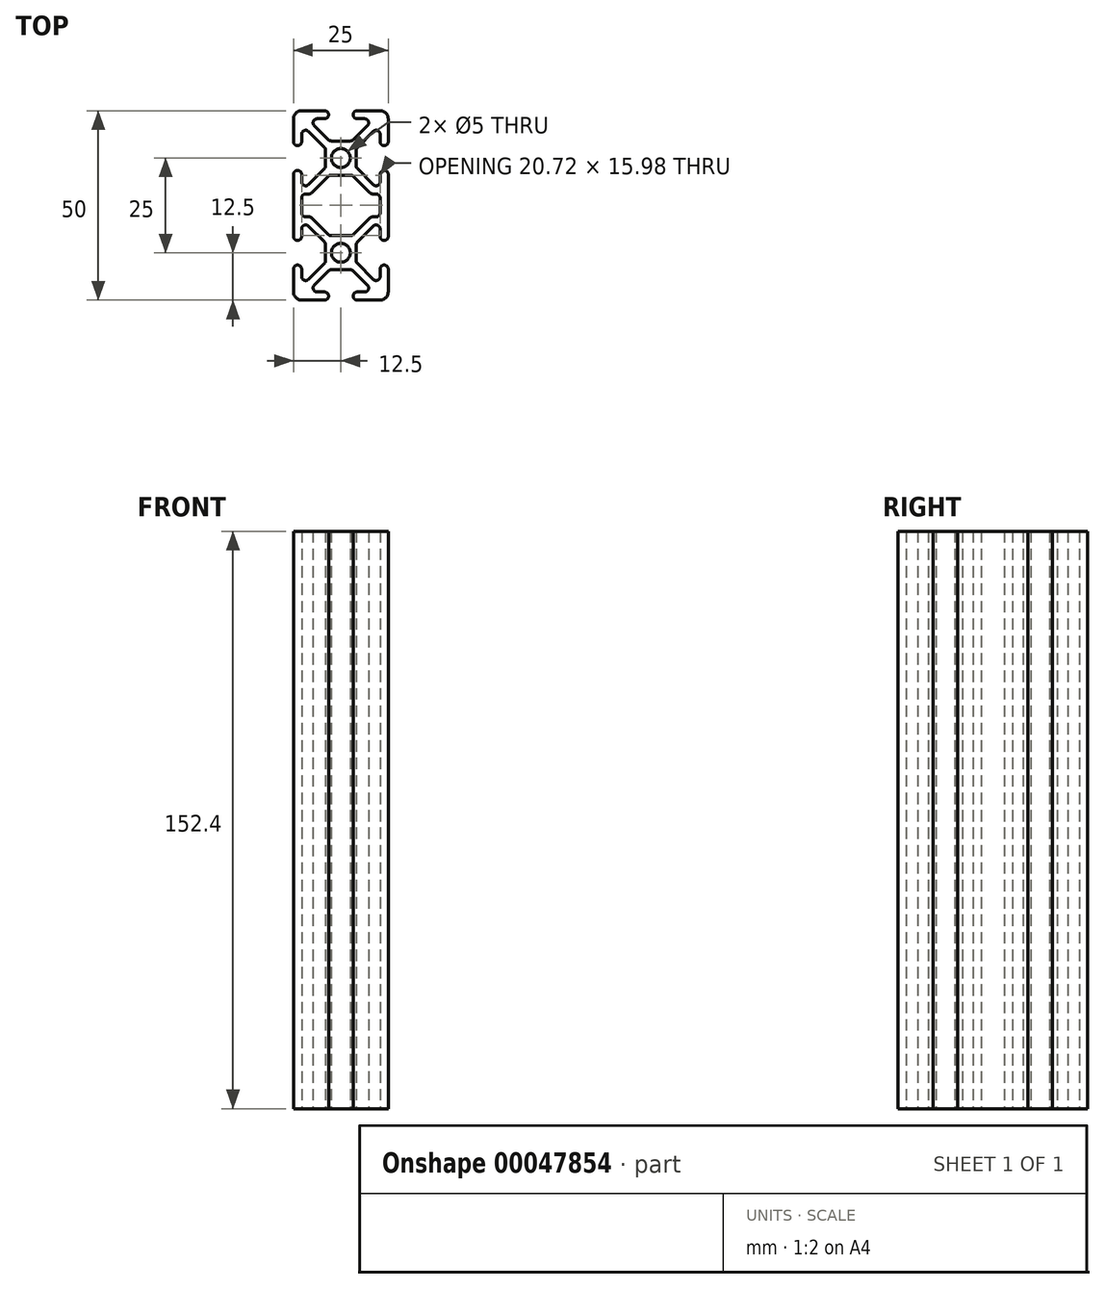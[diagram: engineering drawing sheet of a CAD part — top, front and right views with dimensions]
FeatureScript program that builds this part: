
annotation { "Feature Type Name" : "Feature", "Feature Type Description" : "" }
export const myFeature = defineFeature(function(context is Context, id is Id, definition is map)
    precondition{}
    {
        {
            var Q0;
            Q0=qCreatedBy(makeId("Top.planeOp"),FACE);
            var sketch = newSketch(context, id + "F0", { "sketchPlane" : qUnion([Q0])});
            skCircle(sketch, "E0", {"center": v(0, 0) * mm, "radius": 2.5 * mm});
            skLineSegment(sketch, "E1", {"start": v(0, 0) * mm, "end": v(0, 4.5) * mm, "construction": true});
            skLineSegment(sketch, "E2", {"start": v(0, 0) * mm, "end": v(-4.05, 0) * mm, "construction": true});
            skLineSegment(sketch, "E3", {"start": v(0, 0) * mm, "end": v(-12.5, 12.5) * mm, "construction": true});
            skLineSegment(sketch, "E4", {"start": v(-12.5, 10.36) * mm, "end": v(-12.5, 4.32) * mm});
            skLineSegment(sketch, "E5", {"start": v(-10.36, 12.5) * mm, "end": v(-4.32, 12.5) * mm});
            skLineSegment(sketch, "E6", {"start": v(-4.32, 10.36) * mm, "end": v(-6.26, 10.36) * mm});
            skLineSegment(sketch, "E7", {"start": v(-10.36, 6.26) * mm, "end": v(-10.36, 4.32) * mm});
            skArc(sketch, "E8", {"start": v(-4.32, 12.5) * mm, "mid": v(-3.25, 11.43) * mm, "end": v(-4.32, 10.36) * mm});
            skArc(sketch, "E9", {"start": v(-10.36, 4.32) * mm, "mid": v(-11.43, 3.25) * mm, "end": v(-12.5, 4.32) * mm});
            skLineSegment(sketch, "E10", {"start": v(0, 4.5) * mm, "end": v(-2.55, 4.5) * mm});
            skLineSegment(sketch, "E11", {"start": v(-4.05, 2.1) * mm, "end": v(-4.05, 0) * mm});
            skLineSegment(sketch, "E12", {"start": v(-8.53, 7.02) * mm, "end": v(-4.36, 2.85) * mm});
            skLineSegment(sketch, "E13", {"start": v(-7.02, 8.53) * mm, "end": v(-3.31, 4.82) * mm});
            skLineSegment(sketch, "E14.0.MirrorCS", {"start": v(10.36, 6.26) * mm, "end": v(10.36, 4.32) * mm});
            skLineSegment(sketch, "E14.1.MirrorCS", {"start": v(7.02, 8.53) * mm, "end": v(3.31, 4.82) * mm});
            skArc(sketch, "E14.2.MirrorCS", {"start": v(4.32, 12.5) * mm, "mid": v(3.25, 11.43) * mm, "end": v(4.32, 10.36) * mm});
            skArc(sketch, "E14.3.MirrorCS", {"start": v(10.36, 4.32) * mm, "mid": v(11.43, 3.25) * mm, "end": v(12.5, 4.32) * mm});
            skLineSegment(sketch, "E14.4.MirrorCS", {"start": v(10.36, 12.5) * mm, "end": v(4.32, 12.5) * mm});
            skLineSegment(sketch, "E14.5.MirrorCS", {"start": v(4.32, 10.36) * mm, "end": v(6.26, 10.36) * mm});
            skLineSegment(sketch, "E14.6.MirrorCS", {"start": v(12.5, 10.36) * mm, "end": v(12.5, 4.32) * mm});
            skLineSegment(sketch, "E14.7.MirrorCS", {"start": v(8.53, 7.02) * mm, "end": v(4.36, 2.85) * mm});
            skLineSegment(sketch, "E15.0.MirrorCS", {"start": v(0, 4.5) * mm, "end": v(2.55, 4.5) * mm});
            skLineSegment(sketch, "E16.0.MirrorCS", {"start": v(4.05, 2.1) * mm, "end": v(4.05, 0) * mm});
            skLineSegment(sketch, "E17.1.MirrorCS", {"start": v(12.5, -12.5) * mm, "end": v(12.5, -4.32) * mm});
            skLineSegment(sketch, "E17.5.MirrorCS", {"start": v(10.36, -6.26) * mm, "end": v(10.36, -4.32) * mm});
            skLineSegment(sketch, "E17.6.MirrorCS", {"start": v(8.53, -7.02) * mm, "end": v(4.36, -2.85) * mm});
            skArc(sketch, "E17.10.MirrorCS", {"start": v(10.36, -4.32) * mm, "mid": v(11.43, -3.25) * mm, "end": v(12.5, -4.32) * mm});
            skLineSegment(sketch, "E17.11.MirrorCS", {"start": v(-12.5, -12.5) * mm, "end": v(-12.5, -4.32) * mm});
            skLineSegment(sketch, "E17.14.MirrorCS", {"start": v(-8.53, -7.02) * mm, "end": v(-4.36, -2.85) * mm});
            skArc(sketch, "E17.15.MirrorCS", {"start": v(-10.36, -4.32) * mm, "mid": v(-11.43, -3.25) * mm, "end": v(-12.5, -4.32) * mm});
            skLineSegment(sketch, "E17.16.MirrorCS", {"start": v(-10.36, -6.26) * mm, "end": v(-10.36, -4.32) * mm});
            skLineSegment(sketch, "E18.0.MirrorCS", {"start": v(4.05, -2.1) * mm, "end": v(4.05, 0) * mm});
            skLineSegment(sketch, "E19.0.MirrorCS", {"start": v(-4.05, -2.1) * mm, "end": v(-4.05, 0) * mm});
            skPoint(sketch, "E20.visualSharp", {"position": v(-12.5, 12.5) * mm});
            skArc(sketch, "E20.filletArc", {"start": v(-10.36, 12.5) * mm, "mid": v(-11.87, 11.87) * mm, "end": v(-12.5, 10.36) * mm});
            skPoint(sketch, "E21.visualSharp", {"position": v(12.5, 12.5) * mm});
            skArc(sketch, "E21.filletArc", {"start": v(12.5, 10.36) * mm, "mid": v(11.87, 11.87) * mm, "end": v(10.36, 12.5) * mm});
            skPoint(sketch, "E22.visualSharp", {"position": v(-12.5, -12.5) * mm});
            skPoint(sketch, "E23.visualSharp", {"position": v(4.05, 4.5) * mm});
            skPoint(sketch, "E24.visualSharp", {"position": v(-10.36, 8.85) * mm});
            skArc(sketch, "E24.filletArc", {"start": v(-8.53, 7.02) * mm, "mid": v(-9.7, 7.25) * mm, "end": v(-10.36, 6.26) * mm});
            skPoint(sketch, "E25.visualSharp", {"position": v(-8.85, 10.36) * mm});
            skArc(sketch, "E25.filletArc", {"start": v(-6.26, 10.36) * mm, "mid": v(-7.25, 9.7) * mm, "end": v(-7.02, 8.53) * mm});
            skPoint(sketch, "E26.visualSharp", {"position": v(8.85, 10.36) * mm});
            skArc(sketch, "E26.filletArc", {"start": v(7.02, 8.53) * mm, "mid": v(7.25, 9.7) * mm, "end": v(6.26, 10.36) * mm});
            skArc(sketch, "E27.filletArc", {"start": v(10.36, 6.26) * mm, "mid": v(9.7, 7.25) * mm, "end": v(8.53, 7.02) * mm});
            skArc(sketch, "E28.filletArc", {"start": v(8.53, -7.02) * mm, "mid": v(9.7, -7.25) * mm, "end": v(10.36, -6.26) * mm});
            skArc(sketch, "E29.filletArc", {"start": v(-10.36, -6.26) * mm, "mid": v(-9.7, -7.25) * mm, "end": v(-8.53, -7.02) * mm});
            skPoint(sketch, "E30.orphan", {"position": v(-4.05, 4.5) * mm});
            skPoint(sketch, "E31.visualSharp", {"position": v(-3, 4.5) * mm});
            skArc(sketch, "E31.filletArc", {"start": v(-3.31, 4.82) * mm, "mid": v(-2.96, 4.6) * mm, "end": v(-2.55, 4.5) * mm});
            skPoint(sketch, "E32.visualSharp", {"position": v(3, 4.5) * mm});
            skArc(sketch, "E32.filletArc", {"start": v(2.55, 4.5) * mm, "mid": v(2.96, 4.6) * mm, "end": v(3.31, 4.82) * mm});
            skPoint(sketch, "E33.visualSharp", {"position": v(-4.05, 2.54) * mm});
            skArc(sketch, "E33.filletArc", {"start": v(-4.05, 2.1) * mm, "mid": v(-4.13, 2.5) * mm, "end": v(-4.36, 2.85) * mm});
            skPoint(sketch, "E34.visualSharp", {"position": v(-4.05, -2.54) * mm});
            skArc(sketch, "E34.filletArc", {"start": v(-4.36, -2.85) * mm, "mid": v(-4.13, -2.5) * mm, "end": v(-4.05, -2.1) * mm});
            skPoint(sketch, "E35.visualSharp", {"position": v(4.05, -2.54) * mm});
            skArc(sketch, "E35.filletArc", {"start": v(4.05, -2.1) * mm, "mid": v(4.13, -2.5) * mm, "end": v(4.36, -2.85) * mm});
            skPoint(sketch, "E36.visualSharp", {"position": v(4.05, 2.54) * mm});
            skArc(sketch, "E36.filletArc", {"start": v(4.36, 2.85) * mm, "mid": v(4.13, 2.5) * mm, "end": v(4.05, 2.1) * mm});
            skCircle(sketch, "E37", {"center": v(0, -25) * mm, "radius": 2.5 * mm});
            skLineSegment(sketch, "E38", {"start": v(0, 0) * mm, "end": v(0, -25) * mm, "construction": true});
            skLineSegment(sketch, "E39", {"start": v(0, -12.5) * mm, "end": v(3.65, -12.5) * mm, "construction": true});
            skArc(sketch, "E40.0.MirrorCS", {"start": v(2.55, -29.51) * mm, "mid": v(2.96, -29.6) * mm, "end": v(3.31, -29.82) * mm});
            skArc(sketch, "E40.1.MirrorCS", {"start": v(4.36, -27.85) * mm, "mid": v(4.13, -27.5) * mm, "end": v(4.05, -27.1) * mm});
            skArc(sketch, "E40.2.MirrorCS", {"start": v(-4.05, -27.1) * mm, "mid": v(-4.13, -27.5) * mm, "end": v(-4.36, -27.85) * mm});
            skArc(sketch, "E40.3.MirrorCS", {"start": v(-4.36, -22.15) * mm, "mid": v(-4.13, -22.5) * mm, "end": v(-4.05, -22.9) * mm});
            skArc(sketch, "E40.4.MirrorCS", {"start": v(-3.31, -29.82) * mm, "mid": v(-2.96, -29.6) * mm, "end": v(-2.55, -29.51) * mm});
            skArc(sketch, "E40.5.MirrorCS", {"start": v(4.05, -22.9) * mm, "mid": v(4.13, -22.5) * mm, "end": v(4.36, -22.15) * mm});
            skPoint(sketch, "E40.6.MirrorP", {"position": v(-4.05, -27.54) * mm});
            skPoint(sketch, "E40.7.MirrorP", {"position": v(-10.36, -33.85) * mm});
            skPoint(sketch, "E40.8.MirrorP", {"position": v(4.05, -27.54) * mm});
            skLineSegment(sketch, "E40.10.MirrorCS", {"start": v(0, -25) * mm, "end": v(0, -29.51) * mm, "construction": true});
            skLineSegment(sketch, "E40.11.MirrorCS", {"start": v(-12.5, -35.36) * mm, "end": v(-12.5, -29.32) * mm});
            skLineSegment(sketch, "E40.12.MirrorCS", {"start": v(0, -25) * mm, "end": v(-12.5, -37.5) * mm, "construction": true});
            skLineSegment(sketch, "E40.13.MirrorCS", {"start": v(-4.32, -35.36) * mm, "end": v(-6.26, -35.36) * mm});
            skLineSegment(sketch, "E40.14.MirrorCS", {"start": v(-10.36, -31.26) * mm, "end": v(-10.36, -29.32) * mm});
            skLineSegment(sketch, "E40.15.MirrorCS", {"start": v(0, -29.51) * mm, "end": v(-2.55, -29.51) * mm});
            skPoint(sketch, "E40.16.MirrorP", {"position": v(10.36, -33.85) * mm});
            skLineSegment(sketch, "E40.17.MirrorCS", {"start": v(-4.05, -22.9) * mm, "end": v(-4.05, -25) * mm});
            skLineSegment(sketch, "E40.18.MirrorCS", {"start": v(-8.53, -32.02) * mm, "end": v(-4.36, -27.85) * mm});
            skArc(sketch, "E40.19.MirrorCS", {"start": v(10.36, -29.32) * mm, "mid": v(11.43, -28.25) * mm, "end": v(12.5, -29.32) * mm});
            skArc(sketch, "E40.20.MirrorCS", {"start": v(8.53, -17.98) * mm, "mid": v(9.7, -17.75) * mm, "end": v(10.36, -18.74) * mm});
            skLineSegment(sketch, "E40.21.MirrorCS", {"start": v(-4.05, -27.1) * mm, "end": v(-4.05, -25) * mm});
            skLineSegment(sketch, "E40.22.MirrorCS", {"start": v(12.5, -12.5) * mm, "end": v(12.5, -20.68) * mm});
            skLineSegment(sketch, "E40.23.MirrorCS", {"start": v(8.53, -32.02) * mm, "end": v(4.36, -27.85) * mm});
            skPoint(sketch, "E40.24.MirrorP", {"position": v(-8.85, -35.36) * mm});
            skArc(sketch, "E40.25.MirrorCS", {"start": v(-6.26, -35.36) * mm, "mid": v(-7.25, -34.7) * mm, "end": v(-7.02, -33.53) * mm});
            skArc(sketch, "E40.26.MirrorCS", {"start": v(10.36, -20.68) * mm, "mid": v(11.43, -21.75) * mm, "end": v(12.5, -20.68) * mm});
            skPoint(sketch, "E40.28.MirrorP", {"position": v(-3, -29.51) * mm});
            skLineSegment(sketch, "E40.29.MirrorCS", {"start": v(10.36, -31.26) * mm, "end": v(10.36, -29.32) * mm});
            skLineSegment(sketch, "E40.30.MirrorCS", {"start": v(7.02, -33.53) * mm, "end": v(3.31, -29.82) * mm});
            skPoint(sketch, "E40.31.MirrorP", {"position": v(12.5, -37.5) * mm});
            skLineSegment(sketch, "E40.32.MirrorCS", {"start": v(-10.36, -18.74) * mm, "end": v(-10.36, -20.68) * mm});
            skArc(sketch, "E40.33.MirrorCS", {"start": v(12.5, -35.36) * mm, "mid": v(11.87, -36.87) * mm, "end": v(10.36, -37.5) * mm});
            skArc(sketch, "E40.35.MirrorCS", {"start": v(-10.36, -37.5) * mm, "mid": v(-11.87, -36.87) * mm, "end": v(-12.5, -35.36) * mm});
            skPoint(sketch, "E40.37.MirrorP", {"position": v(-4.05, -22.46) * mm});
            skPoint(sketch, "E40.38.MirrorP", {"position": v(8.85, -35.36) * mm});
            skArc(sketch, "E40.39.MirrorCS", {"start": v(10.36, -31.26) * mm, "mid": v(9.7, -32.25) * mm, "end": v(8.53, -32.02) * mm});
            skLineSegment(sketch, "E40.40.MirrorCS", {"start": v(-8.53, -17.98) * mm, "end": v(-4.36, -22.15) * mm});
            skLineSegment(sketch, "E40.42.MirrorCS", {"start": v(8.53, -17.98) * mm, "end": v(4.36, -22.15) * mm});
            skLineSegment(sketch, "E40.43.MirrorCS", {"start": v(4.05, -22.9) * mm, "end": v(4.05, -25) * mm});
            skArc(sketch, "E40.44.MirrorCS", {"start": v(4.32, -37.5) * mm, "mid": v(3.25, -36.43) * mm, "end": v(4.32, -35.36) * mm});
            skArc(sketch, "E40.45.MirrorCS", {"start": v(-10.36, -18.74) * mm, "mid": v(-9.7, -17.75) * mm, "end": v(-8.53, -17.98) * mm});
            skLineSegment(sketch, "E40.46.MirrorCS", {"start": v(10.36, -18.74) * mm, "end": v(10.36, -20.68) * mm});
            skPoint(sketch, "E40.47.MirrorP", {"position": v(3, -29.51) * mm});
            skPoint(sketch, "E40.48.MirrorP", {"position": v(-4.05, -29.51) * mm});
            skLineSegment(sketch, "E40.49.MirrorCS", {"start": v(0, -29.51) * mm, "end": v(2.55, -29.51) * mm});
            skArc(sketch, "E40.51.MirrorCS", {"start": v(7.02, -33.53) * mm, "mid": v(7.25, -34.7) * mm, "end": v(6.26, -35.36) * mm});
            skPoint(sketch, "E40.52.MirrorP", {"position": v(-12.5, -37.5) * mm});
            skArc(sketch, "E40.53.MirrorCS", {"start": v(-10.36, -20.68) * mm, "mid": v(-11.43, -21.75) * mm, "end": v(-12.5, -20.68) * mm});
            skLineSegment(sketch, "E40.54.MirrorCS", {"start": v(0, -25) * mm, "end": v(-4.05, -25) * mm, "construction": true});
            skLineSegment(sketch, "E40.55.MirrorCS", {"start": v(-10.36, -37.5) * mm, "end": v(-4.32, -37.5) * mm});
            skArc(sketch, "E40.56.MirrorCS", {"start": v(-4.32, -37.5) * mm, "mid": v(-3.25, -36.43) * mm, "end": v(-4.32, -35.36) * mm});
            skArc(sketch, "E40.57.MirrorCS", {"start": v(-10.36, -29.32) * mm, "mid": v(-11.43, -28.25) * mm, "end": v(-12.5, -29.32) * mm});
            skPoint(sketch, "E40.58.MirrorP", {"position": v(4.05, -29.51) * mm});
            skLineSegment(sketch, "E40.59.MirrorCS", {"start": v(-7.02, -33.53) * mm, "end": v(-3.31, -29.82) * mm});
            skLineSegment(sketch, "E40.60.MirrorCS", {"start": v(10.36, -37.5) * mm, "end": v(4.32, -37.5) * mm});
            skLineSegment(sketch, "E40.61.MirrorCS", {"start": v(4.05, -27.1) * mm, "end": v(4.05, -25) * mm});
            skPoint(sketch, "E40.62.MirrorP", {"position": v(4.05, -22.46) * mm});
            skArc(sketch, "E40.63.MirrorCS", {"start": v(-8.53, -32.02) * mm, "mid": v(-9.7, -32.25) * mm, "end": v(-10.36, -31.26) * mm});
            skLineSegment(sketch, "E40.64.MirrorCS", {"start": v(12.5, -35.36) * mm, "end": v(12.5, -29.32) * mm});
            skLineSegment(sketch, "E40.65.MirrorCS", {"start": v(-12.5, -12.5) * mm, "end": v(-12.5, -20.68) * mm});
            skLineSegment(sketch, "E40.67.MirrorCS", {"start": v(4.32, -35.36) * mm, "end": v(6.26, -35.36) * mm});
            skLineSegment(sketch, "E41.0.MirrorCS", {"start": v(0, -4.5) * mm, "end": v(-2.55, -4.5) * mm});
            skPoint(sketch, "E42.visualSharp", {"position": v(-2.55, -4.5) * mm});
            skLineSegment(sketch, "E43", {"start": v(-10.36, -10.54) * mm, "end": v(-10.36, -12.5) * mm});
            skLineSegment(sketch, "E44", {"start": v(-9.3, -9.47) * mm, "end": v(-8.4, -9.47) * mm});
            skLineSegment(sketch, "E45", {"start": v(-3.31, -4.82) * mm, "end": v(-7.65, -9.16) * mm});
            skPoint(sketch, "E46.visualSharp", {"position": v(-3, -4.5) * mm});
            skArc(sketch, "E46.filletArc", {"start": v(-2.55, -4.5) * mm, "mid": v(-2.96, -4.6) * mm, "end": v(-3.31, -4.82) * mm});
            skPoint(sketch, "E47.visualSharp", {"position": v(-7.96, -9.47) * mm});
            skArc(sketch, "E47.filletArc", {"start": v(-8.4, -9.47) * mm, "mid": v(-8, -9.4) * mm, "end": v(-7.65, -9.16) * mm});
            skPoint(sketch, "E48.visualSharp", {"position": v(-10.36, -9.47) * mm});
            skArc(sketch, "E48.filletArc", {"start": v(-9.3, -9.47) * mm, "mid": v(-10.05, -9.79) * mm, "end": v(-10.36, -10.54) * mm});
            skLineSegment(sketch, "E49.0.MirrorCS", {"start": v(0, -4.5) * mm, "end": v(2.55, -4.5) * mm});
            skArc(sketch, "E50.0.MirrorCS", {"start": v(2.55, -4.5) * mm, "mid": v(2.96, -4.6) * mm, "end": v(3.31, -4.82) * mm});
            skLineSegment(sketch, "E51.0.MirrorCS", {"start": v(3.31, -4.82) * mm, "end": v(7.65, -9.16) * mm});
            skPoint(sketch, "E52.0.MirrorP", {"position": v(7.96, -9.47) * mm});
            skArc(sketch, "E53.0.MirrorCS", {"start": v(8.4, -9.47) * mm, "mid": v(8, -9.4) * mm, "end": v(7.65, -9.16) * mm});
            skLineSegment(sketch, "E54.0.MirrorCS", {"start": v(9.3, -9.47) * mm, "end": v(8.4, -9.47) * mm});
            skArc(sketch, "E55.0.MirrorCS", {"start": v(9.3, -9.47) * mm, "mid": v(10.05, -9.79) * mm, "end": v(10.36, -10.54) * mm});
            skLineSegment(sketch, "E56.0.MirrorCS", {"start": v(10.36, -10.54) * mm, "end": v(10.36, -12.5) * mm});
            skLineSegment(sketch, "E57.0.MirrorCS", {"start": v(10.36, -14.46) * mm, "end": v(10.36, -12.5) * mm});
            skArc(sketch, "E58.0.MirrorCS", {"start": v(9.3, -15.53) * mm, "mid": v(10.05, -15.21) * mm, "end": v(10.36, -14.46) * mm});
            skLineSegment(sketch, "E59.0.MirrorCS", {"start": v(9.3, -15.53) * mm, "end": v(8.4, -15.53) * mm});
            skArc(sketch, "E60.0.MirrorCS", {"start": v(8.4, -15.53) * mm, "mid": v(8, -15.6) * mm, "end": v(7.65, -15.84) * mm});
            skLineSegment(sketch, "E61.0.MirrorCS", {"start": v(3.31, -20.18) * mm, "end": v(7.65, -15.84) * mm});
            skArc(sketch, "E62.0.MirrorCS", {"start": v(2.55, -20.5) * mm, "mid": v(2.96, -20.4) * mm, "end": v(3.31, -20.18) * mm});
            skLineSegment(sketch, "E63.0.MirrorCS", {"start": v(0, -20.5) * mm, "end": v(2.55, -20.5) * mm});
            skLineSegment(sketch, "E64.0.MirrorCS", {"start": v(0, -20.5) * mm, "end": v(-2.55, -20.5) * mm});
            skArc(sketch, "E65.0.MirrorCS", {"start": v(-2.55, -20.5) * mm, "mid": v(-2.96, -20.4) * mm, "end": v(-3.31, -20.18) * mm});
            skLineSegment(sketch, "E66.0.MirrorCS", {"start": v(-3.31, -20.18) * mm, "end": v(-7.65, -15.84) * mm});
            skArc(sketch, "E67.0.MirrorCS", {"start": v(-8.4, -15.53) * mm, "mid": v(-8, -15.6) * mm, "end": v(-7.65, -15.84) * mm});
            skLineSegment(sketch, "E68.0.MirrorCS", {"start": v(-9.3, -15.53) * mm, "end": v(-8.4, -15.53) * mm});
            skArc(sketch, "E69.0.MirrorCS", {"start": v(-9.3, -15.53) * mm, "mid": v(-10.05, -15.21) * mm, "end": v(-10.36, -14.46) * mm});
            skLineSegment(sketch, "E70.0.MirrorCS", {"start": v(-10.36, -14.46) * mm, "end": v(-10.36, -12.5) * mm});
            skSolve(sketch);
        }
        {
            var Q0;
            Q0=makeQuery(id+"F0.imprint","IMPRINT",FACE,{"disambiguationData":[TD([[makeQuery(id+"F0.imprint","IMPRINT",EDGE,{"derivedFrom":sQuery(id+"F0.wireOp",EDGE,"E0")}),-1.0]])]});
            extrude(context, id + "F1", {"entities" : qUnion([Q0]), "depth" : 152.4 * mm});
        }
    });
